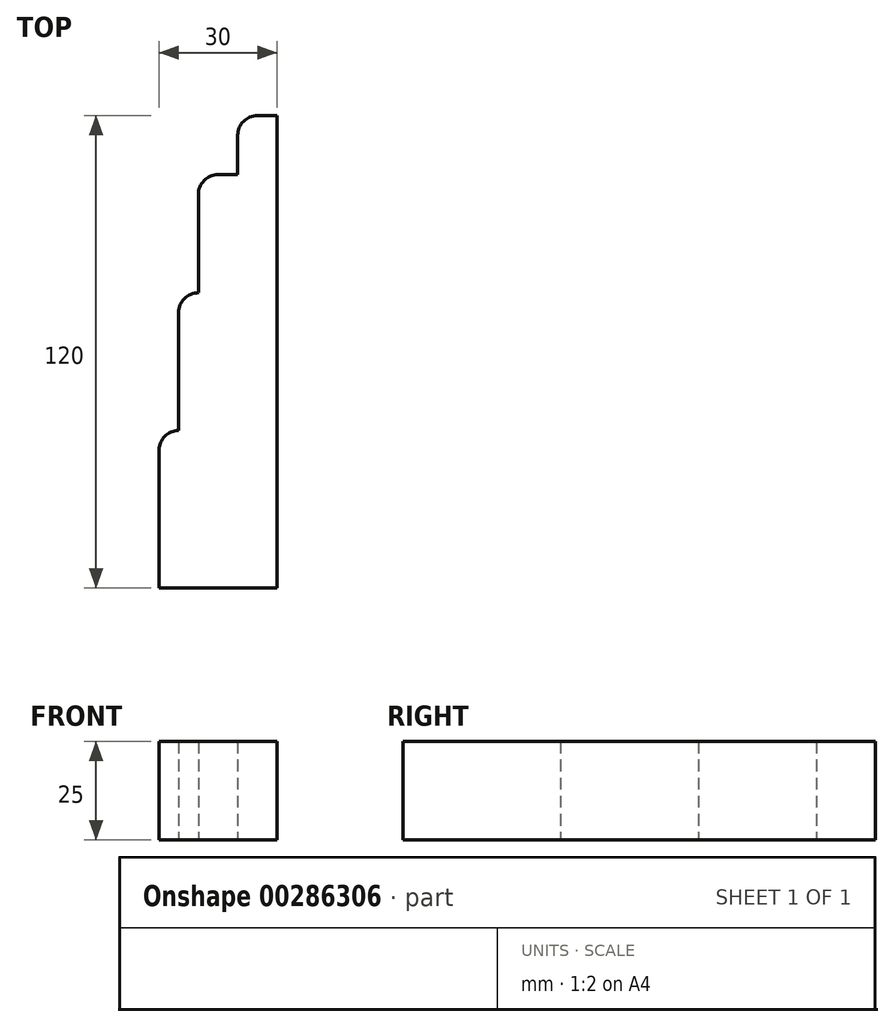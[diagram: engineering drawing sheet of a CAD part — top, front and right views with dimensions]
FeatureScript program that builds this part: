
annotation { "Feature Type Name" : "Feature", "Feature Type Description" : "" }
export const myFeature = defineFeature(function(context is Context, id is Id, definition is map)
    precondition{}
    {
        {
            var Q0;
            Q0=qCreatedBy(makeId("Top.planeOp"),FACE);
            var sketch = newSketch(context, id + "F0", { "sketchPlane" : qUnion([Q0])});
            skLineSegment(sketch, "E0", {"start": v(0, 0) * mm, "end": v(0, 35) * mm});
            skLineSegment(sketch, "E1", {"start": v(5, 40) * mm, "end": v(5, 40) * mm});
            skLineSegment(sketch, "E2", {"start": v(5, 40) * mm, "end": v(5, 70) * mm});
            skLineSegment(sketch, "E3", {"start": v(10, 75) * mm, "end": v(10, 75) * mm});
            skLineSegment(sketch, "E4", {"start": v(10, 75) * mm, "end": v(10, 100) * mm});
            skLineSegment(sketch, "E5", {"start": v(15, 105) * mm, "end": v(20, 105) * mm});
            skLineSegment(sketch, "E6", {"start": v(20, 105) * mm, "end": v(20, 115) * mm});
            skLineSegment(sketch, "E7", {"start": v(25, 120) * mm, "end": v(30, 120) * mm});
            skLineSegment(sketch, "E8", {"start": v(30, 120) * mm, "end": v(30, 0) * mm});
            skLineSegment(sketch, "E9", {"start": v(30, 0) * mm, "end": v(0, 0) * mm});
            skPoint(sketch, "E10.visualSharp", {"position": v(20, 120) * mm});
            skArc(sketch, "E10.filletArc", {"start": v(25, 120) * mm, "mid": v(21.46, 118.54) * mm, "end": v(20, 115) * mm});
            skPoint(sketch, "E11.visualSharp", {"position": v(10, 105) * mm});
            skArc(sketch, "E11.filletArc", {"start": v(15, 105) * mm, "mid": v(11.46, 103.54) * mm, "end": v(10, 100) * mm});
            skPoint(sketch, "E12.visualSharp", {"position": v(5, 75) * mm});
            skArc(sketch, "E12.filletArc", {"start": v(10, 75) * mm, "mid": v(6.46, 73.54) * mm, "end": v(5, 70) * mm});
            skPoint(sketch, "E13.visualSharp", {"position": v(0, 40) * mm});
            skArc(sketch, "E13.filletArc", {"start": v(5, 40) * mm, "mid": v(1.46, 38.54) * mm, "end": v(0, 35) * mm});
            skSolve(sketch);
        }
        {
            var Q0;
            Q0 = qSketchRegion(id + "F0", true);
            extrude(context, id + "F1", {"entities" : qUnion([Q0]), "depth" : 25 * mm});
        }
    });
